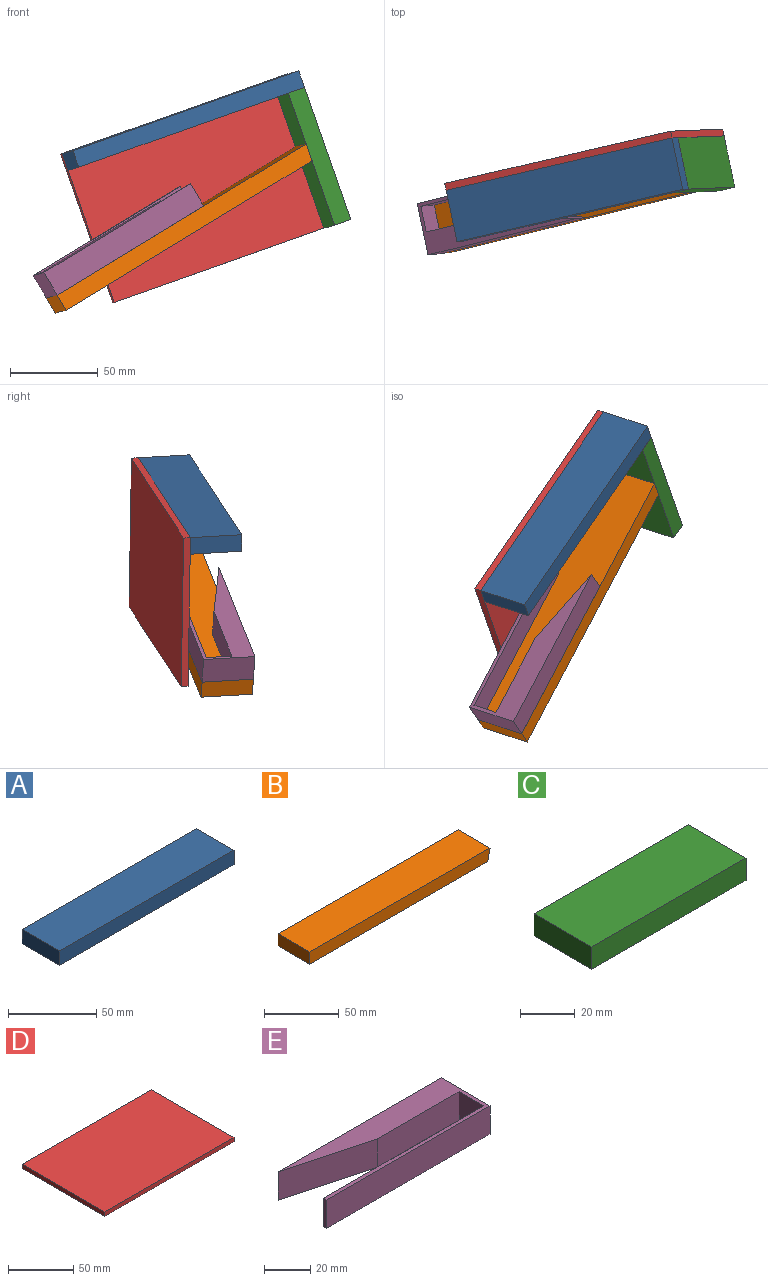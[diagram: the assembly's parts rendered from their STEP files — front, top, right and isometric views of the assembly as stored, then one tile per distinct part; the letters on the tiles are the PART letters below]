
ASSEMBLY  parts=5 mates=11
PART A: 6 faces, bbox 140x30x10 mm
  f0: plane 140x10mm, normal (0,1,0), area 1400mm2, adj f1,f3,f4,f5
  f1: plane 30x10mm, normal (-1,0,0), area 300mm2, adj f0,f2,f4,f5
  f2: plane 140x10mm, normal (0,-1,0), area 1400mm2, adj f1,f3,f4,f5
  f3: plane 30x10mm, normal (1,0,0), area 300mm2, adj f0,f2,f4,f5
  f4: plane 140x30mm, normal (0,0,1), area 4200mm2, adj f0,f1,f2,f3
  f5: plane 140x30mm, normal (0,0,-1), area 4200mm2, adj f0,f1,f2,f3
PART B: 6 faces, bbox 170x30x10 mm
  f0: plane 170x10mm, normal (0,1,0), area 1689.8mm2, adj f1,f2,f4,f5
  f1: plane 167.95x30mm, normal (0,0,-1), area 5038.6mm2, adj f0,f2,f3,f5
  f2: plane 30x10mm, normal (-1,0,0), area 300mm2, adj f0,f1,f3,f4
  f3: plane 170x10mm, normal (0,-1,0), area 1689.8mm2, adj f1,f2,f4,f5
  f4: plane 170x30mm, normal (0,0,1), area 5100mm2, adj f0,f2,f3,f5
  f5: plane 30x10mm, normal (0.98,0,-0.2), area 306.2mm2, adj f0,f1,f3,f4
PART C: 6 faces, bbox 80x30x10 mm
  f0: plane 80x10mm, normal (0,1,0), area 800mm2, adj f1,f3,f4,f5
  f1: plane 30x10mm, normal (-1,0,0), area 300mm2, adj f0,f2,f4,f5
  f2: plane 80x10mm, normal (0,-1,0), area 800mm2, adj f1,f3,f4,f5
  f3: plane 30x10mm, normal (1,0,0), area 300mm2, adj f0,f2,f4,f5
  f4: plane 80x30mm, normal (0,0,1), area 2400mm2, adj f0,f1,f2,f3
  f5: plane 80x30mm, normal (0,0,-1), area 2400mm2, adj f0,f1,f2,f3
PART D: 6 faces, bbox 140x90x4 mm
  f0: plane 140x4mm, normal (0,1,0), area 560mm2, adj f1,f3,f4,f5
  f1: plane 90x4mm, normal (-1,0,0), area 360mm2, adj f0,f2,f4,f5
  f2: plane 140x4mm, normal (0,-1,0), area 560mm2, adj f1,f3,f4,f5
  f3: plane 90x4mm, normal (1,0,0), area 360mm2, adj f0,f2,f4,f5
  f4: plane 140x90mm, normal (0,0,1), area 12600mm2, adj f0,f1,f2,f3
  f5: plane 140x90mm, normal (0,0,-1), area 12600mm2, adj f0,f1,f2,f3
PART E: 10 faces, bbox 100x30x15 mm
  f0: plane 100x15mm, normal (0,1,0), area 1500mm2, adj f1,f7,f8,f9
  f1: plane 48x15mm, normal (-0.26,-0.97,0), area 745.9mm2, adj f0,f2,f8,f9
  f2: plane 50x15mm, normal (0,-1,0), area 750mm2, adj f1,f3,f8,f9
  f3: plane 15x15mm, normal (-1,0,0), area 225mm2, adj f2,f4,f8,f9
  f4: plane 98x15mm, normal (0,1,0), area 1470mm2, adj f3,f5,f8,f9
  f5: plane 15x2mm, normal (-1,0,0), area 30mm2, adj f4,f6,f8,f9
  f6: plane 100x15mm, normal (0,-1,0), area 1500mm2, adj f5,f7,f8,f9
  f7: plane 30x15mm, normal (1,0,0), area 450mm2, adj f0,f6,f8,f9
  f8: plane 100x30mm, normal (0,0,1), area 1218mm2, adj f0,f1,f2,f3,f4,f5,f6,f7
  f9: plane 100x30mm, normal (0,0,-1), area 1218mm2, adj f0,f1,f2,f3,f4,f5,f6,f7
PLACE A rot(axis=(0.17,-0.01,-0.99),167.8deg) t=(46.21,-49.26,-0.05)mm
PLACE B rot(axis=(0,-0.93,0.37),33.3deg) t=(59.41,102.1,-50.32)mm
PLACE C rot(axis=(0.81,0.07,-0.58),170.5deg) t=(174.23,-25.97,-63.25)mm
PLACE D rot(axis=(-0.19,0.7,0.69),175.1deg) t=(24.94,37.56,3.43)mm
PLACE E rot(axis=(0.27,0,-0.96),167.7deg) t=(65.27,15.25,-41.02)mm
MATE planar D.f1 <-> C.f5  axis (0.92,0.21,0.33) through (133.29,61.92,-4.87)mm
MATE planar A.f5 <-> C.f1  axis (0.33,0.02,-0.94) through (60.74,29.9,6.3)mm
MATE planar E.f6 <-> B.f0  axis (-0.21,0.98,-0.06) through (18.92,32.72,-58.55)mm
MATE planar D.f5 <-> C.f2  axis (0.21,-0.98,0.06) through (69.22,45.09,-27.57)mm
MATE planar B.f5 <-> C.f4  axis (0.92,0.21,0.33) through (127.84,43.2,-7.94)mm
MATE planar D.f0 <-> A.f4  axis (-0.33,-0.02,0.94) through (53.94,46.36,14.78)mm
MATE planar E.f7 <-> B.f2  axis (-0.84,-0.21,-0.51) through (-19.81,7.8,-83.13)mm
MATE planar A.f2 <-> C.f2  axis (-0.21,0.98,-0.06) through (56.01,44.48,10.18)mm
MATE planar B.f0 <-> C.f2  axis (-0.21,0.98,-0.06) through (54.11,40.51,-51.74)mm
MATE planar E.f9 <-> B.f4  axis (0.51,0.06,-0.86) through (6.99,11.82,-75.73)mm
MATE planar C.f5 <-> A.f1  axis (0.92,0.21,0.33) through (138.44,45.39,-8.64)mm
